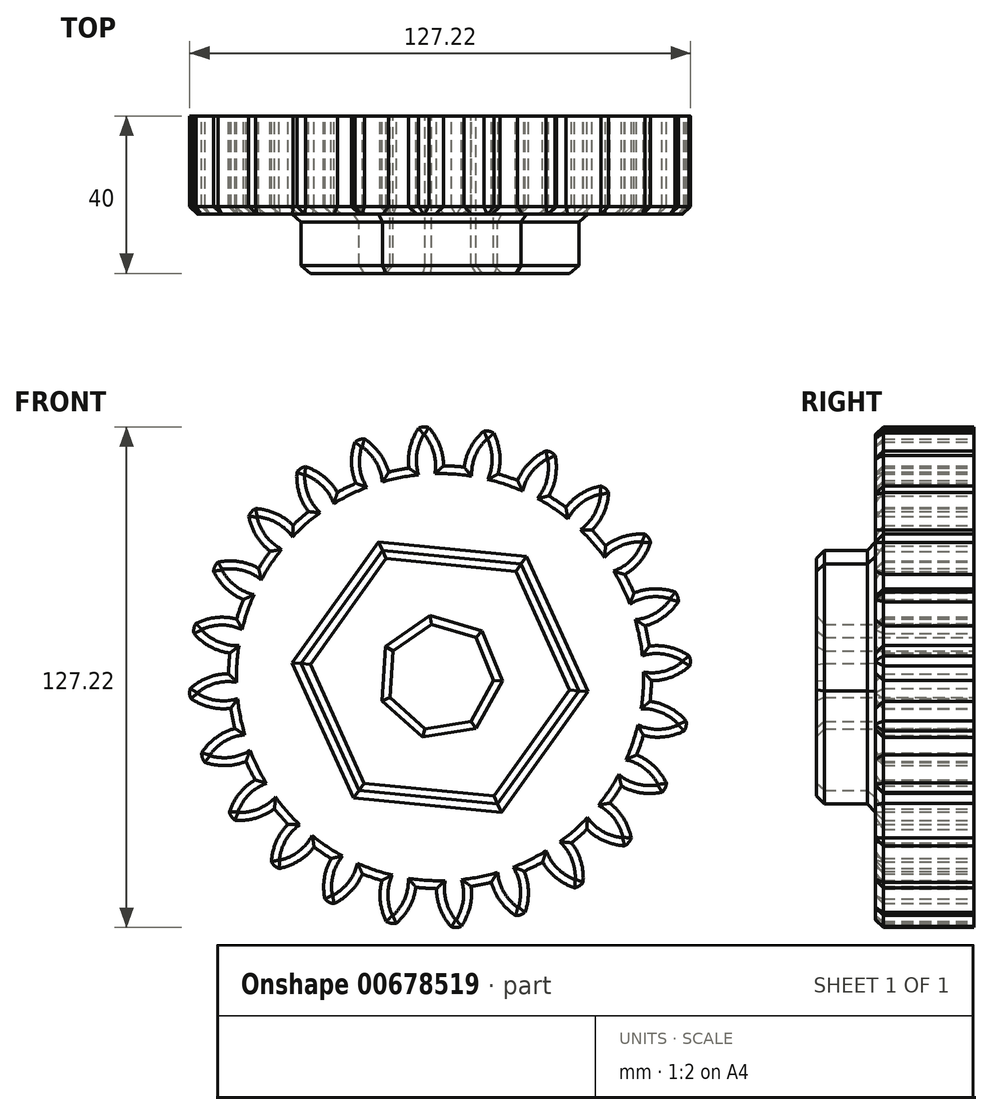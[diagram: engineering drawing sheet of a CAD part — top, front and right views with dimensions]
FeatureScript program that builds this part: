
annotation { "Feature Type Name" : "Feature", "Feature Type Description" : "" }
export const myFeature = defineFeature(function(context is Context, id is Id, definition is map)
    precondition{}
    {
        {
            var Q0;
            Q0=qCreatedBy(makeId("Front.planeOp"),FACE);
            var sketch = newSketch(context, id + "F0", { "sketchPlane" : qUnion([Q0])});
            skCircle(sketch, "E0", {"center": v(0, 0) * mm, "radius": 53.72 * mm});
            skCircle(sketch, "E1", {"center": v(0, 0) * mm, "radius": 58.67 * mm, "construction": true});
            skCircle(sketch, "E2", {"center": v(0, 0) * mm, "radius": 63.5 * mm, "construction": true});
            skLineSegment(sketch, "E3", {"start": v(0, 0) * mm, "end": v(0, 100.95) * mm, "construction": true});
            skLineSegment(sketch, "E4", {"start": v(0, 0) * mm, "end": v(-5.95, 90.82) * mm, "construction": true});
            skLineSegment(sketch, "E5", {"start": v(0, 58.67) * mm, "end": v(-49.43, 58.67) * mm, "construction": true});
            skLineSegment(sketch, "E6", {"start": v(0, 58.67) * mm, "end": v(-58.4, 37.42) * mm, "construction": true});
            skCircle(sketch, "E7", {"center": v(0, 0) * mm, "radius": 55.14 * mm, "construction": true});
            skCircle(sketch, "E8", {"center": v(0, 58.67) * mm, "radius": 14.6 * mm, "construction": true});
            skCircle(sketch, "E9", {"center": v(-13.72, 53.68) * mm, "radius": 14.6 * mm, "construction": true});
            skArc(sketch, "E10", {"start": v(0, 58.67) * mm, "mid": v(-1.2, 61.19) * mm, "end": v(-2.86, 63.44) * mm});
            skArc(sketch, "E11", {"start": v(0.88, 53.71) * mm, "mid": v(0.67, 56.23) * mm, "end": v(0, 58.67) * mm});
            skArc(sketch, "E12.MirrorCS", {"start": v(-7.66, 58.17) * mm, "mid": v(-6.79, 60.82) * mm, "end": v(-5.45, 63.27) * mm});
            skArc(sketch, "E13.MirrorCS", {"start": v(-7.88, 53.14) * mm, "mid": v(-8, 55.67) * mm, "end": v(-7.66, 58.17) * mm});
            skArc(sketch, "E14", {"start": v(-2.86, 63.44) * mm, "mid": v(-4.17, 63.6) * mm, "end": v(-5.45, 63.27) * mm});
            skCircle(sketch, "E15.cCircle", {"center": v(0, 0) * mm, "radius": 30.67 * mm, "construction": true});
            skLineSegment(sketch, "E15.0", {"start": v(-20.6, -28.8) * mm, "end": v(-35.25, 3.45) * mm});
            skLineSegment(sketch, "E15.1", {"start": v(-35.25, 3.45) * mm, "end": v(-14.64, 32.25) * mm});
            skLineSegment(sketch, "E15.2", {"start": v(-14.64, 32.25) * mm, "end": v(20.6, 28.8) * mm});
            skLineSegment(sketch, "E15.3", {"start": v(20.6, 28.8) * mm, "end": v(35.25, -3.45) * mm});
            skLineSegment(sketch, "E15.4", {"start": v(35.25, -3.45) * mm, "end": v(14.64, -32.25) * mm});
            skLineSegment(sketch, "E15.5", {"start": v(14.64, -32.25) * mm, "end": v(-20.6, -28.8) * mm});
            skPoint(sketch, "E15.0.midPoint", {"position": v(-27.93, -12.68) * mm});
            skCircle(sketch, "E16.cCircle", {"center": v(0, 0) * mm, "radius": 12.3 * mm, "construction": true});
            skLineSegment(sketch, "E16.0", {"start": v(-3.88, -13.08) * mm, "end": v(-12.64, -5.13) * mm});
            skLineSegment(sketch, "E16.1", {"start": v(-12.64, -5.13) * mm, "end": v(-11.9, 6.69) * mm});
            skLineSegment(sketch, "E16.2", {"start": v(-11.9, 6.69) * mm, "end": v(-2.19, 13.47) * mm});
            skLineSegment(sketch, "E16.3", {"start": v(-2.19, 13.47) * mm, "end": v(9.17, 10.1) * mm});
            skLineSegment(sketch, "E16.4", {"start": v(9.17, 10.1) * mm, "end": v(13.62, -0.87) * mm});
            skLineSegment(sketch, "E16.5", {"start": v(13.62, -0.87) * mm, "end": v(7.81, -11.19) * mm});
            skLineSegment(sketch, "E16.6", {"start": v(7.81, -11.19) * mm, "end": v(-3.88, -13.08) * mm});
            skPoint(sketch, "E16.0.midPoint", {"position": v(-8.26, -9.1) * mm});
            skSolve(sketch);
        }
        {
            var Q0;
            {var subQ0=sQuery(id+"F0.wireOp",EDGE,"E0");var subQ1=makeQuery(id+"F0.imprint","INTERSECT",VERTEX,{"derivedFrom":[subQ0,sQuery(id+"F0.wireOp",EDGE,"E11")]});Q0=makeQuery(id+"F0.imprint","IMPRINT",FACE,{"disambiguationData":[TD([[makeQuery(id+"F0.imprint","IMPRINT",EDGE,{"disambiguationData":[TD([[subQ1,-1.0]])],"derivedFrom":subQ0}),1.0]])]});}
            var Q1;
            Q1=makeQuery(id+"F0.imprint","IMPRINT",FACE,{"disambiguationData":[TD([[makeQuery(id+"F0.imprint","IMPRINT",EDGE,{"derivedFrom":sQuery(id+"F0.wireOp",EDGE,"E10")}),1.0]])]});
            extrude(context, id + "F1", {"entities" : qUnion([Q0, Q1]), "depth" : 25 * mm, "offsetDistance" : 25 * mm});
        }
        {
            var Q0;
            Q0=makeQuery(id+"F1.opExtrude","SWEPT_BODY",BODY,{"disambiguationData":[OSD([sQuery(id+"F0.wireOp",EDGE,"E0"),sQuery(id+"F0.wireOp",EDGE,"E10"),sQuery(id+"F0.wireOp",EDGE,"E11"),sQuery(id+"F0.wireOp",EDGE,"E12.MirrorCS"),sQuery(id+"F0.wireOp",EDGE,"E13.MirrorCS"),sQuery(id+"F0.wireOp",EDGE,"E14")])]});
            var Q1;
            Q1=makeQuery(id+"F1.opExtrude","SWEPT_FACE",FACE,{"disambiguationData":[OSD([sQuery(id+"F0.wireOp",EDGE,"E0")])]});
            circularPattern(context, id + "F2", {"entities" : qUnion([Q0]), "axis" : qUnion([Q1]), "angle" : 360 * degree, "instanceCount" : 24, "equalSpace" : true});
        }
        {
            var Q0;
            Q0=makeQuery(id+"F0.imprint","IMPRINT",FACE,{"disambiguationData":[TD([[makeQuery(id+"F0.imprint","IMPRINT",EDGE,{"derivedFrom":sQuery(id+"F0.wireOp",EDGE,"E15.0")}),-1.0]])]});
            extrude(context, id + "F3", {"entities" : qUnion([Q0]), "operationType" : NewBodyOperationType.ADD, "depth" : 40 * mm, "offsetDistance" : 25 * mm});
        }
        {
            var Q0;
            {var subQ0=makeQuery(id+"F1.opExtrude","CAP_FACE",FACE,{"disambiguationData":[OSD([sQuery(id+"F0.wireOp",EDGE,"E0"),sQuery(id+"F0.wireOp",EDGE,"E10"),sQuery(id+"F0.wireOp",EDGE,"E11"),sQuery(id+"F0.wireOp",EDGE,"E12.MirrorCS"),sQuery(id+"F0.wireOp",EDGE,"E13.MirrorCS"),sQuery(id+"F0.wireOp",EDGE,"E14"),sQuery(id+"F0.wireOp",EDGE,"E15.0"),sQuery(id+"F0.wireOp",EDGE,"E15.1"),sQuery(id+"F0.wireOp",EDGE,"E15.2"),sQuery(id+"F0.wireOp",EDGE,"E15.3"),sQuery(id+"F0.wireOp",EDGE,"E15.4"),sQuery(id+"F0.wireOp",EDGE,"E15.5")])],"isStart":false});Q0=makeQuery(id+"F3.boolean.opBoolean","MERGE",FACE,{"derivedFrom":[subQ0,makeQuery(id+"F2.opPattern","COPY",FACE,{"derivedFrom":subQ0,"instanceName":"1"}),makeQuery(id+"F2.opPattern","COPY",FACE,{"derivedFrom":subQ0,"instanceName":"2"}),makeQuery(id+"F2.opPattern","COPY",FACE,{"derivedFrom":subQ0,"instanceName":"3"}),makeQuery(id+"F2.opPattern","COPY",FACE,{"derivedFrom":subQ0,"instanceName":"4"}),makeQuery(id+"F2.opPattern","COPY",FACE,{"derivedFrom":subQ0,"instanceName":"5"}),makeQuery(id+"F2.opPattern","COPY",FACE,{"derivedFrom":subQ0,"instanceName":"6"}),makeQuery(id+"F2.opPattern","COPY",FACE,{"derivedFrom":subQ0,"instanceName":"7"}),makeQuery(id+"F2.opPattern","COPY",FACE,{"derivedFrom":subQ0,"instanceName":"8"}),makeQuery(id+"F2.opPattern","COPY",FACE,{"derivedFrom":subQ0,"instanceName":"9"}),makeQuery(id+"F2.opPattern","COPY",FACE,{"derivedFrom":subQ0,"instanceName":"10"}),makeQuery(id+"F2.opPattern","COPY",FACE,{"derivedFrom":subQ0,"instanceName":"11"}),makeQuery(id+"F2.opPattern","COPY",FACE,{"derivedFrom":subQ0,"instanceName":"12"}),makeQuery(id+"F2.opPattern","COPY",FACE,{"derivedFrom":subQ0,"instanceName":"13"}),makeQuery(id+"F2.opPattern","COPY",FACE,{"derivedFrom":subQ0,"instanceName":"14"}),makeQuery(id+"F2.opPattern","COPY",FACE,{"derivedFrom":subQ0,"instanceName":"15"}),makeQuery(id+"F2.opPattern","COPY",FACE,{"derivedFrom":subQ0,"instanceName":"16"}),makeQuery(id+"F2.opPattern","COPY",FACE,{"derivedFrom":subQ0,"instanceName":"17"}),makeQuery(id+"F2.opPattern","COPY",FACE,{"derivedFrom":subQ0,"instanceName":"18"}),makeQuery(id+"F2.opPattern","COPY",FACE,{"derivedFrom":subQ0,"instanceName":"19"}),makeQuery(id+"F2.opPattern","COPY",FACE,{"derivedFrom":subQ0,"instanceName":"20"}),makeQuery(id+"F2.opPattern","COPY",FACE,{"derivedFrom":subQ0,"instanceName":"21"}),makeQuery(id+"F2.opPattern","COPY",FACE,{"derivedFrom":subQ0,"instanceName":"22"}),makeQuery(id+"F2.opPattern","COPY",FACE,{"derivedFrom":subQ0,"instanceName":"23"})]});}
            var Q1;
            Q1=makeQuery(id+"F3.opExtrude","CAP_FACE",FACE,{"disambiguationData":[OSD([sQuery(id+"F0.wireOp",EDGE,"E15.0"),sQuery(id+"F0.wireOp",EDGE,"E15.1"),sQuery(id+"F0.wireOp",EDGE,"E15.2"),sQuery(id+"F0.wireOp",EDGE,"E15.3"),sQuery(id+"F0.wireOp",EDGE,"E15.4"),sQuery(id+"F0.wireOp",EDGE,"E15.5"),sQuery(id+"F0.wireOp",EDGE,"E16.0"),sQuery(id+"F0.wireOp",EDGE,"E16.1"),sQuery(id+"F0.wireOp",EDGE,"E16.2"),sQuery(id+"F0.wireOp",EDGE,"E16.3"),sQuery(id+"F0.wireOp",EDGE,"E16.4"),sQuery(id+"F0.wireOp",EDGE,"E16.5"),sQuery(id+"F0.wireOp",EDGE,"E16.6")])],"isStart":false});
            chamfer(context, id + "F4", {"entities" : qUnion([Q0, Q1]), "width" : 2 * mm, "tangentPropagation" : true});
        }
    });
